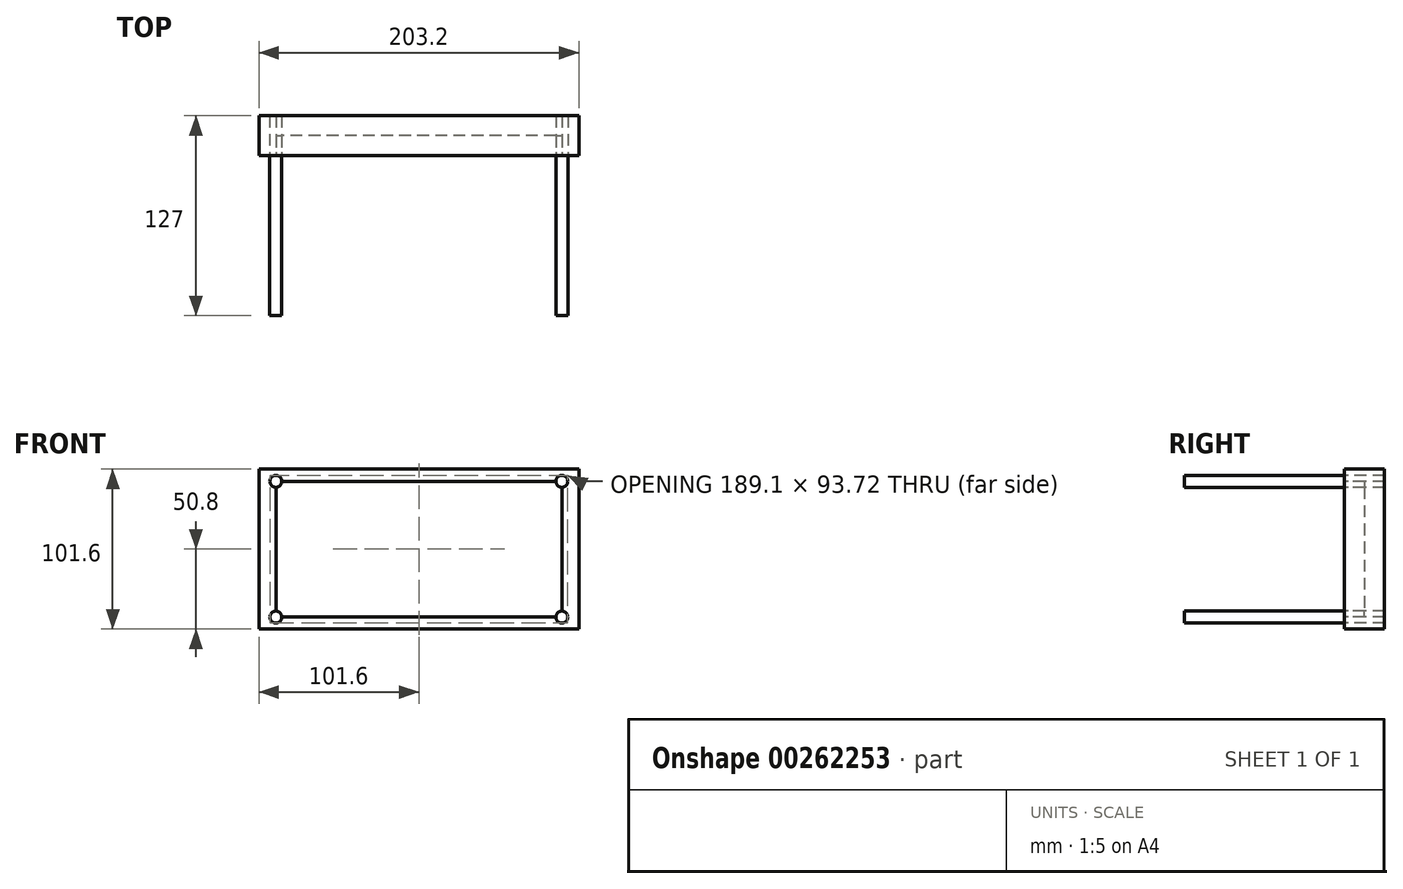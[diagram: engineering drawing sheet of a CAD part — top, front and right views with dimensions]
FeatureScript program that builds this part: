
annotation { "Feature Type Name" : "Feature", "Feature Type Description" : "" }
export const myFeature = defineFeature(function(context is Context, id is Id, definition is map)
    precondition{}
    {
        {
            var Q0;
            Q0=qCreatedBy(makeId("Front.planeOp"),FACE);
            var sketch = newSketch(context, id + "F0", { "sketchPlane" : qUnion([Q0])});
            skLineSegment(sketch, "E0.bottom", {"start": v(101.6, 50.8) * mm, "end": v(-101.6, 50.8) * mm});
            skLineSegment(sketch, "E0.top", {"start": v(101.6, -50.8) * mm, "end": v(-101.6, -50.8) * mm});
            skLineSegment(sketch, "E0.left", {"start": v(101.6, 50.8) * mm, "end": v(101.6, -50.8) * mm});
            skLineSegment(sketch, "E0.right", {"start": v(-101.6, 50.8) * mm, "end": v(-101.6, -50.8) * mm});
            skPoint(sketch, "E0.middle", {"position": v(0, 0) * mm});
            skLineSegment(sketch, "E1.bottom", {"start": v(90.81, 43.12) * mm, "end": v(-90.81, 43.12) * mm});
            skLineSegment(sketch, "E1.top", {"start": v(90.81, -43.12) * mm, "end": v(-90.81, -43.12) * mm});
            skLineSegment(sketch, "E1.left", {"start": v(90.81, 43.12) * mm, "end": v(90.81, -43.12) * mm});
            skLineSegment(sketch, "E1.right", {"start": v(-90.81, 43.12) * mm, "end": v(-90.81, -43.12) * mm});
            skCircle(sketch, "E2", {"center": v(-90.81, 43.12) * mm, "radius": 3.81 * mm});
            skCircle(sketch, "E3", {"center": v(90.81, 43.12) * mm, "radius": 3.81 * mm});
            skCircle(sketch, "E4", {"center": v(90.81, -43.12) * mm, "radius": 3.81 * mm});
            skCircle(sketch, "E5", {"center": v(-90.81, -43.12) * mm, "radius": 3.81 * mm});
            skSolve(sketch);
        }
        {
            var Q0;
            Q0 = qSketchRegion(id + "F0", true);
            extrude(context, id + "F1", {"entities" : qUnion([Q0]), "oppositeDirection" : true, "depth" : 25.4 * mm});
        }
        {
            var Q0;
            {var subQ0=sQuery(id+"F0.wireOp",EDGE,"E1.right");var subQ1=sQuery(id+"F0.wireOp",EDGE,"E1.bottom");var subQ2=makeQuery(id+"F0.imprint","INTERSECT",VERTEX,{"derivedFrom":[subQ1,subQ0]});Q0=makeQuery(id+"F0.imprint","IMPRINT",FACE,{"disambiguationData":[TD([[makeQuery(id+"F0.imprint","IMPRINT",EDGE,{"disambiguationData":[TD([[subQ2,1.0]])],"derivedFrom":subQ1}),-1.0]])]});}
            var Q1;
            {var subQ0=sQuery(id+"F0.wireOp",EDGE,"E1.right");var subQ1=sQuery(id+"F0.wireOp",EDGE,"E1.bottom");var subQ2=makeQuery(id+"F0.imprint","INTERSECT",VERTEX,{"derivedFrom":[subQ1,subQ0]});Q1=makeQuery(id+"F0.imprint","IMPRINT",FACE,{"disambiguationData":[TD([[makeQuery(id+"F0.imprint","IMPRINT",EDGE,{"disambiguationData":[TD([[subQ2,1.0]])],"derivedFrom":subQ1}),1.0]])]});}
            var Q2;
            {var subQ0=sQuery(id+"F0.wireOp",EDGE,"E1.right");var subQ1=sQuery(id+"F0.wireOp",EDGE,"E1.top");var subQ2=makeQuery(id+"F0.imprint","INTERSECT",VERTEX,{"derivedFrom":[subQ1,subQ0]});Q2=makeQuery(id+"F0.imprint","IMPRINT",FACE,{"disambiguationData":[TD([[makeQuery(id+"F0.imprint","IMPRINT",EDGE,{"disambiguationData":[TD([[subQ2,1.0]])],"derivedFrom":subQ1}),-1.0]])]});}
            var Q3;
            {var subQ0=sQuery(id+"F0.wireOp",EDGE,"E1.right");var subQ1=sQuery(id+"F0.wireOp",EDGE,"E1.top");var subQ2=makeQuery(id+"F0.imprint","INTERSECT",VERTEX,{"derivedFrom":[subQ1,subQ0]});Q3=makeQuery(id+"F0.imprint","IMPRINT",FACE,{"disambiguationData":[TD([[makeQuery(id+"F0.imprint","IMPRINT",EDGE,{"disambiguationData":[TD([[subQ2,1.0]])],"derivedFrom":subQ1}),1.0]])]});}
            var Q4;
            {var subQ0=sQuery(id+"F0.wireOp",EDGE,"E1.left");var subQ1=sQuery(id+"F0.wireOp",EDGE,"E1.top");var subQ2=makeQuery(id+"F0.imprint","INTERSECT",VERTEX,{"derivedFrom":[subQ1,subQ0]});Q4=makeQuery(id+"F0.imprint","IMPRINT",FACE,{"disambiguationData":[TD([[makeQuery(id+"F0.imprint","IMPRINT",EDGE,{"disambiguationData":[TD([[subQ2,-1.0]])],"derivedFrom":subQ1}),1.0]])]});}
            var Q5;
            {var subQ0=sQuery(id+"F0.wireOp",EDGE,"E1.left");var subQ1=sQuery(id+"F0.wireOp",EDGE,"E1.top");var subQ2=makeQuery(id+"F0.imprint","INTERSECT",VERTEX,{"derivedFrom":[subQ1,subQ0]});Q5=makeQuery(id+"F0.imprint","IMPRINT",FACE,{"disambiguationData":[TD([[makeQuery(id+"F0.imprint","IMPRINT",EDGE,{"disambiguationData":[TD([[subQ2,-1.0]])],"derivedFrom":subQ1}),-1.0]])]});}
            var Q6;
            {var subQ0=sQuery(id+"F0.wireOp",EDGE,"E1.left");var subQ1=sQuery(id+"F0.wireOp",EDGE,"E1.bottom");var subQ2=makeQuery(id+"F0.imprint","INTERSECT",VERTEX,{"derivedFrom":[subQ1,subQ0]});Q6=makeQuery(id+"F0.imprint","IMPRINT",FACE,{"disambiguationData":[TD([[makeQuery(id+"F0.imprint","IMPRINT",EDGE,{"disambiguationData":[TD([[subQ2,-1.0]])],"derivedFrom":subQ1}),1.0]])]});}
            var Q7;
            {var subQ0=sQuery(id+"F0.wireOp",EDGE,"E1.left");var subQ1=sQuery(id+"F0.wireOp",EDGE,"E1.bottom");var subQ2=makeQuery(id+"F0.imprint","INTERSECT",VERTEX,{"derivedFrom":[subQ1,subQ0]});Q7=makeQuery(id+"F0.imprint","IMPRINT",FACE,{"disambiguationData":[TD([[makeQuery(id+"F0.imprint","IMPRINT",EDGE,{"disambiguationData":[TD([[subQ2,-1.0]])],"derivedFrom":subQ1}),-1.0]])]});}
            extrude(context, id + "F2", {"entities" : qUnion([Q0, Q1, Q2, Q3, Q4, Q5, Q6, Q7]), "depth" : 101.6 * mm});
        }
        {
            var Q0;
            {var subQ5=sQuery(id+"F0.wireOp",EDGE,"E3");var subQ6=sQuery(id+"F0.wireOp",EDGE,"E1.bottom");var subQ7=makeQuery(id+"F0.imprint","INTERSECT",VERTEX,{"derivedFrom":[subQ6,subQ5]});Q0=makeQuery(id+"F0.imprint","IMPRINT",FACE,{"disambiguationData":[TD([[makeQuery(id+"F0.imprint","IMPRINT",EDGE,{"disambiguationData":[TD([[subQ7,-1.0]])],"derivedFrom":subQ6}),1.0]])]});}
            extrude(context, id + "F3", {"entities" : qUnion([Q0]), "oppositeDirection" : true, "depth" : 12.7 * mm});
        }
        {
            var Q0;
            {var subQ0=sQuery(id+"F0.wireOp",EDGE,"E1.right");var subQ1=sQuery(id+"F0.wireOp",EDGE,"E1.top");var subQ2=makeQuery(id+"F0.imprint","INTERSECT",VERTEX,{"derivedFrom":[subQ1,subQ0]});Q0=makeQuery(id+"F0.imprint","IMPRINT",FACE,{"disambiguationData":[TD([[makeQuery(id+"F0.imprint","IMPRINT",EDGE,{"disambiguationData":[TD([[subQ2,1.0]])],"derivedFrom":subQ1}),1.0]])]});}
            var Q1;
            {var subQ0=sQuery(id+"F0.wireOp",EDGE,"E1.right");var subQ1=sQuery(id+"F0.wireOp",EDGE,"E1.top");var subQ2=makeQuery(id+"F0.imprint","INTERSECT",VERTEX,{"derivedFrom":[subQ1,subQ0]});Q1=makeQuery(id+"F0.imprint","IMPRINT",FACE,{"disambiguationData":[TD([[makeQuery(id+"F0.imprint","IMPRINT",EDGE,{"disambiguationData":[TD([[subQ2,1.0]])],"derivedFrom":subQ1}),-1.0]])]});}
            var Q2;
            {var subQ0=sQuery(id+"F0.wireOp",EDGE,"E1.right");var subQ1=sQuery(id+"F0.wireOp",EDGE,"E1.bottom");var subQ2=makeQuery(id+"F0.imprint","INTERSECT",VERTEX,{"derivedFrom":[subQ1,subQ0]});Q2=makeQuery(id+"F0.imprint","IMPRINT",FACE,{"disambiguationData":[TD([[makeQuery(id+"F0.imprint","IMPRINT",EDGE,{"disambiguationData":[TD([[subQ2,1.0]])],"derivedFrom":subQ1}),-1.0]])]});}
            var Q3;
            {var subQ0=sQuery(id+"F0.wireOp",EDGE,"E1.right");var subQ1=sQuery(id+"F0.wireOp",EDGE,"E1.bottom");var subQ2=makeQuery(id+"F0.imprint","INTERSECT",VERTEX,{"derivedFrom":[subQ1,subQ0]});Q3=makeQuery(id+"F0.imprint","IMPRINT",FACE,{"disambiguationData":[TD([[makeQuery(id+"F0.imprint","IMPRINT",EDGE,{"disambiguationData":[TD([[subQ2,1.0]])],"derivedFrom":subQ1}),1.0]])]});}
            var Q4;
            {var subQ0=sQuery(id+"F0.wireOp",EDGE,"E1.left");var subQ1=sQuery(id+"F0.wireOp",EDGE,"E1.bottom");var subQ2=makeQuery(id+"F0.imprint","INTERSECT",VERTEX,{"derivedFrom":[subQ1,subQ0]});Q4=makeQuery(id+"F0.imprint","IMPRINT",FACE,{"disambiguationData":[TD([[makeQuery(id+"F0.imprint","IMPRINT",EDGE,{"disambiguationData":[TD([[subQ2,-1.0]])],"derivedFrom":subQ1}),-1.0]])]});}
            var Q5;
            {var subQ0=sQuery(id+"F0.wireOp",EDGE,"E1.left");var subQ1=sQuery(id+"F0.wireOp",EDGE,"E1.bottom");var subQ2=makeQuery(id+"F0.imprint","INTERSECT",VERTEX,{"derivedFrom":[subQ1,subQ0]});Q5=makeQuery(id+"F0.imprint","IMPRINT",FACE,{"disambiguationData":[TD([[makeQuery(id+"F0.imprint","IMPRINT",EDGE,{"disambiguationData":[TD([[subQ2,-1.0]])],"derivedFrom":subQ1}),1.0]])]});}
            var Q6;
            {var subQ0=sQuery(id+"F0.wireOp",EDGE,"E1.left");var subQ1=sQuery(id+"F0.wireOp",EDGE,"E1.top");var subQ2=makeQuery(id+"F0.imprint","INTERSECT",VERTEX,{"derivedFrom":[subQ1,subQ0]});Q6=makeQuery(id+"F0.imprint","IMPRINT",FACE,{"disambiguationData":[TD([[makeQuery(id+"F0.imprint","IMPRINT",EDGE,{"disambiguationData":[TD([[subQ2,-1.0]])],"derivedFrom":subQ1}),1.0]])]});}
            var Q7;
            {var subQ0=sQuery(id+"F0.wireOp",EDGE,"E1.left");var subQ1=sQuery(id+"F0.wireOp",EDGE,"E1.top");var subQ2=makeQuery(id+"F0.imprint","INTERSECT",VERTEX,{"derivedFrom":[subQ1,subQ0]});Q7=makeQuery(id+"F0.imprint","IMPRINT",FACE,{"disambiguationData":[TD([[makeQuery(id+"F0.imprint","IMPRINT",EDGE,{"disambiguationData":[TD([[subQ2,-1.0]])],"derivedFrom":subQ1}),-1.0]])]});}
            extrude(context, id + "F4", {"entities" : qUnion([Q0, Q1, Q2, Q3, Q4, Q5, Q6, Q7]), "oppositeDirection" : true, "depth" : 25.4 * mm});
        }
    });
